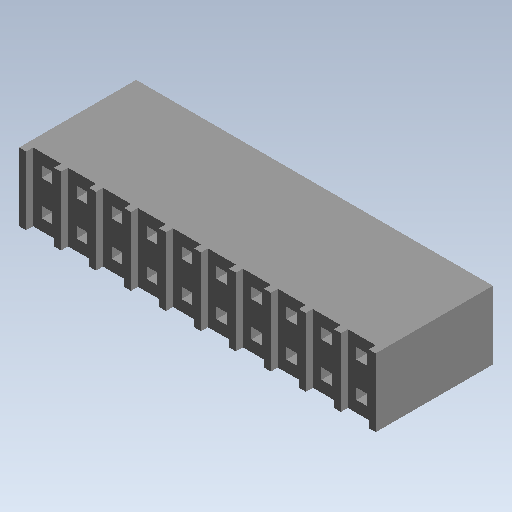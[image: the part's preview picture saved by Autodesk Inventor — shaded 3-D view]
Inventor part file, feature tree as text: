
AUTODESK INVENTOR PART (.ipt)
format: ipt  version: 2021 (Build 250183000, 183)  size: 253,952 bytes
history: native  units: mm (DEFAULTED — no unit token found)
features: other x14, extrude x2, sketch x2
ambient origin geometry x8: Origin, YZ Plane, XZ Plane, XY Plane, X Axis, Y Axis, Z Axis, Center Point
bodies: Solid1 (feature_tree)
feature tree (18):
  extrude  "Extrusion1"  Depth=10.16mm TaperAngle=0.0deg
  extrude  "Extrusion2"  [1 undecoded]
  other  "pin_XY"
  other  "pin_YZ"
  other  "pin_ZX"
  other  "pin_X"
  other  "pin_Y"
  other  "pin_Z"
  other  "pin_Center"
  other  "terminal_XY"
  other  "terminal_YZ"
  other  "terminal_ZX"
  other  "terminal_X"
  other  "terminal_Y"
  other  "terminal_Z"
  other  "terminal_Center"
  sketch  "Sketch_1"  dims[d0=8.509mm d1=0.0mm d2=10.16mm d3=0.0mm]
  sketch  "Sketch_6"  dims[d4=0.0mm d5=0.0mm]
note: 1 required parameter value undecoded (feature->parameter linkage not recoverable at this tier; creation-order binding heuristic only, values carry confidence <= 0.55)
